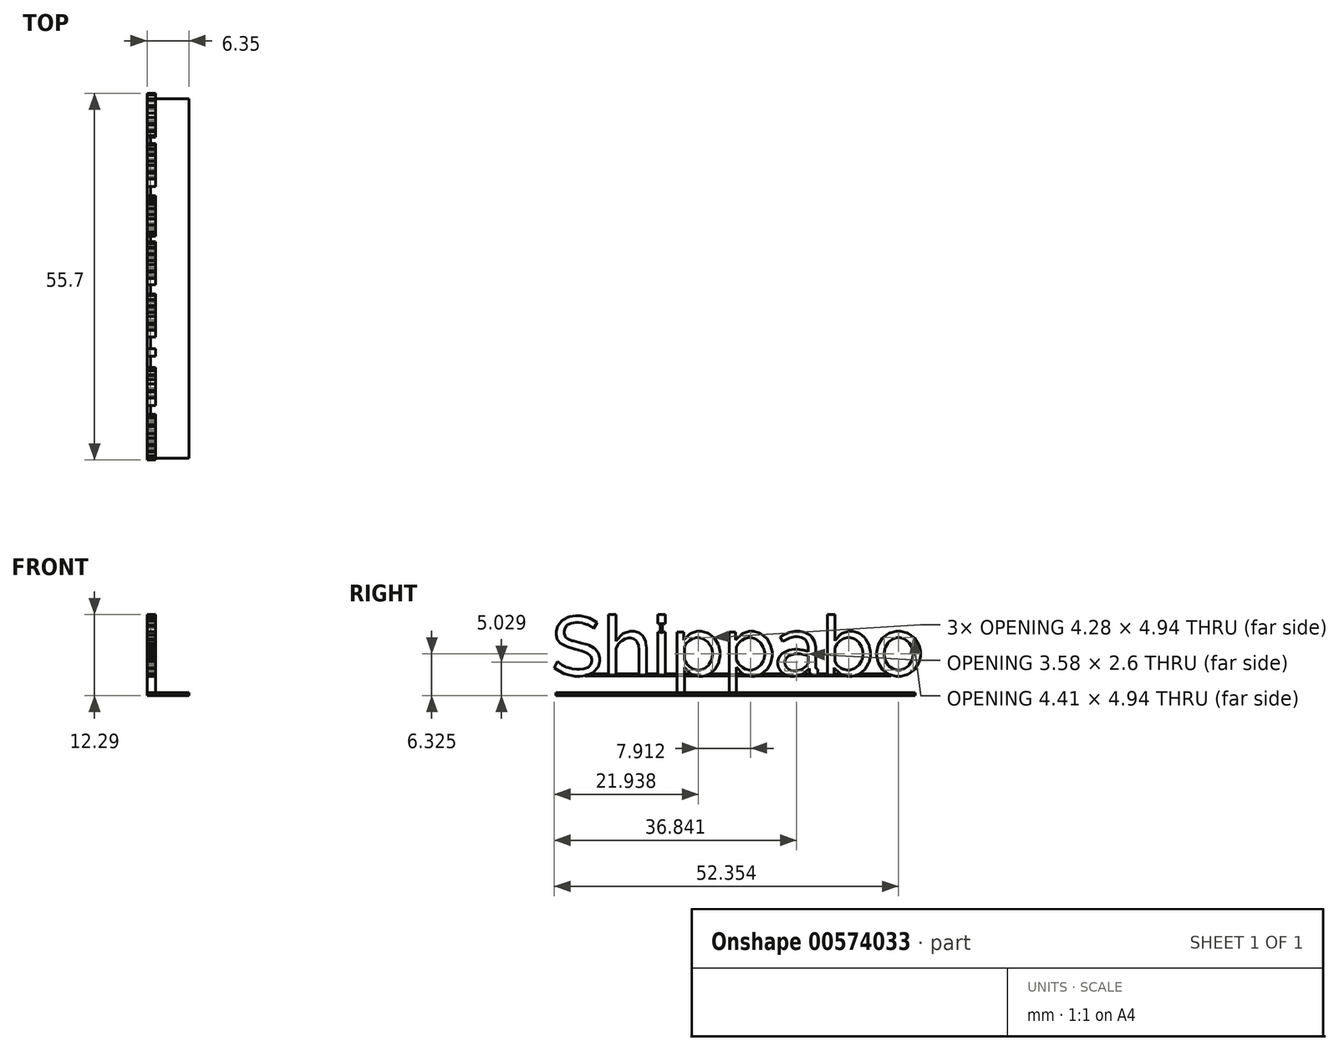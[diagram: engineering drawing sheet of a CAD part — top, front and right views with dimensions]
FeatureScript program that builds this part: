
annotation { "Feature Type Name" : "Feature", "Feature Type Description" : "" }
export const myFeature = defineFeature(function(context is Context, id is Id, definition is map)
    precondition{}
    {
        {
            var Q0;
            Q0=qCreatedBy(makeId("Right.planeOp"),FACE);
            var sketch = newSketch(context, id + "F0", { "sketchPlane" : qUnion([Q0])});
            skLineSegment(sketch, "E0", {"start": v(-21.84, 3.84) * mm, "end": v(-21.87, 3.87) * mm});
            skLineSegment(sketch, "E1", {"start": v(-21.87, 3.87) * mm, "end": v(-22.2, 4.16) * mm});
            skLineSegment(sketch, "E2", {"start": v(-22.2, 4.16) * mm, "end": v(-22.25, 4.18) * mm});
            skLineSegment(sketch, "E3", {"start": v(-22.25, 4.18) * mm, "end": v(-22.3, 4.21) * mm});
            skLineSegment(sketch, "E4", {"start": v(-22.3, 4.21) * mm, "end": v(-22.77, 4.46) * mm});
            skLineSegment(sketch, "E5", {"start": v(-22.77, 4.46) * mm, "end": v(-22.82, 4.48) * mm});
            skLineSegment(sketch, "E6", {"start": v(-22.82, 4.48) * mm, "end": v(-22.88, 4.5) * mm});
            skLineSegment(sketch, "E7", {"start": v(-22.88, 4.5) * mm, "end": v(-23.45, 4.68) * mm});
            skLineSegment(sketch, "E8", {"start": v(-23.45, 4.68) * mm, "end": v(-23.51, 4.7) * mm});
            skLineSegment(sketch, "E9", {"start": v(-23.51, 4.7) * mm, "end": v(-23.58, 4.71) * mm});
            skLineSegment(sketch, "E10", {"start": v(-23.58, 4.71) * mm, "end": v(-24.12, 4.78) * mm});
            skLineSegment(sketch, "E11", {"start": v(-24.12, 4.78) * mm, "end": v(-24.3, 4.78) * mm});
            skLineSegment(sketch, "E12", {"start": v(-24.3, 4.78) * mm, "end": v(-24.52, 4.78) * mm});
            skLineSegment(sketch, "E13", {"start": v(-24.52, 4.78) * mm, "end": v(-25.2, 4.68) * mm});
            skLineSegment(sketch, "E14", {"start": v(-25.2, 4.68) * mm, "end": v(-25.76, 4.45) * mm});
            skLineSegment(sketch, "E15", {"start": v(-25.76, 4.45) * mm, "end": v(-25.84, 4.39) * mm});
            skLineSegment(sketch, "E16", {"start": v(-25.84, 4.39) * mm, "end": v(-25.92, 4.32) * mm});
            skLineSegment(sketch, "E17", {"start": v(-25.92, 4.32) * mm, "end": v(-26.2, 3.92) * mm});
            skLineSegment(sketch, "E18", {"start": v(-26.2, 3.92) * mm, "end": v(-26.33, 3.46) * mm});
            skLineSegment(sketch, "E19", {"start": v(-26.33, 3.46) * mm, "end": v(-26.33, 3.3) * mm});
            skLineSegment(sketch, "E20", {"start": v(-26.33, 3.3) * mm, "end": v(-26.33, 3.16) * mm});
            skLineSegment(sketch, "E21", {"start": v(-26.33, 3.16) * mm, "end": v(-26.21, 2.74) * mm});
            skLineSegment(sketch, "E22", {"start": v(-26.21, 2.74) * mm, "end": v(-26.19, 2.7) * mm});
            skLineSegment(sketch, "E23", {"start": v(-26.19, 2.7) * mm, "end": v(-26.16, 2.66) * mm});
            skLineSegment(sketch, "E24", {"start": v(-26.16, 2.66) * mm, "end": v(-25.8, 2.31) * mm});
            skLineSegment(sketch, "E25", {"start": v(-25.8, 2.31) * mm, "end": v(-25.75, 2.29) * mm});
            skLineSegment(sketch, "E26", {"start": v(-25.75, 2.29) * mm, "end": v(-25.7, 2.26) * mm});
            skLineSegment(sketch, "E27", {"start": v(-25.7, 2.26) * mm, "end": v(-25.08, 2) * mm});
            skLineSegment(sketch, "E28", {"start": v(-25.08, 2) * mm, "end": v(-25, 1.99) * mm});
            skLineSegment(sketch, "E29", {"start": v(-25, 1.99) * mm, "end": v(-24.93, 1.97) * mm});
            skLineSegment(sketch, "E30", {"start": v(-24.93, 1.97) * mm, "end": v(-24.05, 1.74) * mm});
            skLineSegment(sketch, "E31", {"start": v(-24.05, 1.74) * mm, "end": v(-23.95, 1.72) * mm});
            skLineSegment(sketch, "E32", {"start": v(-23.95, 1.72) * mm, "end": v(-23.84, 1.7) * mm});
            skLineSegment(sketch, "E33", {"start": v(-23.84, 1.7) * mm, "end": v(-22.78, 1.4) * mm});
            skLineSegment(sketch, "E34", {"start": v(-22.78, 1.4) * mm, "end": v(-22.69, 1.37) * mm});
            skLineSegment(sketch, "E35", {"start": v(-22.69, 1.37) * mm, "end": v(-22.6, 1.34) * mm});
            skLineSegment(sketch, "E36", {"start": v(-22.6, 1.34) * mm, "end": v(-21.8, 0.93) * mm});
            skLineSegment(sketch, "E37", {"start": v(-21.8, 0.93) * mm, "end": v(-21.72, 0.88) * mm});
            skLineSegment(sketch, "E38", {"start": v(-21.72, 0.88) * mm, "end": v(-21.66, 0.83) * mm});
            skLineSegment(sketch, "E39", {"start": v(-21.66, 0.83) * mm, "end": v(-21.15, 0.24) * mm});
            skLineSegment(sketch, "E40", {"start": v(-21.15, 0.24) * mm, "end": v(-21.11, 0.17) * mm});
            skLineSegment(sketch, "E41", {"start": v(-21.11, 0.17) * mm, "end": v(-21.08, 0.1) * mm});
            skLineSegment(sketch, "E42", {"start": v(-21.08, 0.1) * mm, "end": v(-20.9, -0.62) * mm});
            skLineSegment(sketch, "E43", {"start": v(-20.9, -0.62) * mm, "end": v(-20.9, -0.86) * mm});
            skLineSegment(sketch, "E44", {"start": v(-20.9, -0.86) * mm, "end": v(-20.9, -1.14) * mm});
            skLineSegment(sketch, "E45", {"start": v(-20.9, -1.14) * mm, "end": v(-21.12, -1.9) * mm});
            skLineSegment(sketch, "E46", {"start": v(-21.12, -1.9) * mm, "end": v(-21.16, -1.98) * mm});
            skLineSegment(sketch, "E47", {"start": v(-21.16, -1.98) * mm, "end": v(-21.2, -2.06) * mm});
            skLineSegment(sketch, "E48", {"start": v(-21.2, -2.06) * mm, "end": v(-21.78, -2.72) * mm});
            skLineSegment(sketch, "E49", {"start": v(-21.78, -2.72) * mm, "end": v(-21.85, -2.77) * mm});
            skLineSegment(sketch, "E50", {"start": v(-21.85, -2.77) * mm, "end": v(-21.92, -2.82) * mm});
            skLineSegment(sketch, "E51", {"start": v(-21.92, -2.82) * mm, "end": v(-22.79, -3.2) * mm});
            skLineSegment(sketch, "E52", {"start": v(-22.79, -3.2) * mm, "end": v(-22.89, -3.23) * mm});
            skLineSegment(sketch, "E53", {"start": v(-22.89, -3.23) * mm, "end": v(-22.99, -3.25) * mm});
            skLineSegment(sketch, "E54", {"start": v(-22.99, -3.25) * mm, "end": v(-23.88, -3.37) * mm});
            skLineSegment(sketch, "E55", {"start": v(-23.88, -3.37) * mm, "end": v(-24.18, -3.37) * mm});
            skLineSegment(sketch, "E56", {"start": v(-24.18, -3.37) * mm, "end": v(-24.68, -3.37) * mm});
            skLineSegment(sketch, "E57", {"start": v(-24.68, -3.37) * mm, "end": v(-26, -3.1) * mm});
            skLineSegment(sketch, "E58", {"start": v(-26, -3.1) * mm, "end": v(-26.16, -3.05) * mm});
            skLineSegment(sketch, "E59", {"start": v(-26.16, -3.05) * mm, "end": v(-26.31, -3) * mm});
            skLineSegment(sketch, "E60", {"start": v(-26.31, -3) * mm, "end": v(-27.72, -2.2) * mm});
            skLineSegment(sketch, "E61", {"start": v(-27.72, -2.2) * mm, "end": v(-27.85, -2.1) * mm});
            skLineSegment(sketch, "E62", {"start": v(-27.85, -2.1) * mm, "end": v(-27.3, -1.14) * mm});
            skLineSegment(sketch, "E63", {"start": v(-27.3, -1.14) * mm, "end": v(-27.27, -1.17) * mm});
            skLineSegment(sketch, "E64", {"start": v(-27.27, -1.17) * mm, "end": v(-26.83, -1.53) * mm});
            skLineSegment(sketch, "E65", {"start": v(-26.83, -1.53) * mm, "end": v(-26.78, -1.57) * mm});
            skLineSegment(sketch, "E66", {"start": v(-26.78, -1.57) * mm, "end": v(-26.72, -1.6) * mm});
            skLineSegment(sketch, "E67", {"start": v(-26.72, -1.6) * mm, "end": v(-26.1, -1.93) * mm});
            skLineSegment(sketch, "E68", {"start": v(-26.1, -1.93) * mm, "end": v(-26.04, -1.96) * mm});
            skLineSegment(sketch, "E69", {"start": v(-26.04, -1.96) * mm, "end": v(-25.97, -1.98) * mm});
            skLineSegment(sketch, "E70", {"start": v(-25.97, -1.98) * mm, "end": v(-25.23, -2.22) * mm});
            skLineSegment(sketch, "E71", {"start": v(-25.23, -2.22) * mm, "end": v(-25.15, -2.24) * mm});
            skLineSegment(sketch, "E72", {"start": v(-25.15, -2.24) * mm, "end": v(-25.07, -2.25) * mm});
            skLineSegment(sketch, "E73", {"start": v(-25.07, -2.25) * mm, "end": v(-24.39, -2.34) * mm});
            skLineSegment(sketch, "E74", {"start": v(-24.39, -2.34) * mm, "end": v(-24.16, -2.34) * mm});
            skLineSegment(sketch, "E75", {"start": v(-24.16, -2.34) * mm, "end": v(-23.94, -2.34) * mm});
            skLineSegment(sketch, "E76", {"start": v(-23.94, -2.34) * mm, "end": v(-23.3, -2.26) * mm});
            skLineSegment(sketch, "E77", {"start": v(-23.3, -2.26) * mm, "end": v(-22.75, -2.06) * mm});
            skLineSegment(sketch, "E78", {"start": v(-22.75, -2.06) * mm, "end": v(-22.66, -2) * mm});
            skLineSegment(sketch, "E79", {"start": v(-22.66, -2) * mm, "end": v(-22.57, -1.94) * mm});
            skLineSegment(sketch, "E80", {"start": v(-22.57, -1.94) * mm, "end": v(-22.26, -1.57) * mm});
            skLineSegment(sketch, "E81", {"start": v(-22.26, -1.57) * mm, "end": v(-22.12, -1.12) * mm});
            skLineSegment(sketch, "E82", {"start": v(-22.12, -1.12) * mm, "end": v(-22.12, -0.97) * mm});
            skLineSegment(sketch, "E83", {"start": v(-22.12, -0.97) * mm, "end": v(-22.12, -0.81) * mm});
            skLineSegment(sketch, "E84", {"start": v(-22.12, -0.81) * mm, "end": v(-22.27, -0.37) * mm});
            skLineSegment(sketch, "E85", {"start": v(-22.27, -0.37) * mm, "end": v(-22.3, -0.33) * mm});
            skLineSegment(sketch, "E86", {"start": v(-22.3, -0.33) * mm, "end": v(-22.32, -0.29) * mm});
            skLineSegment(sketch, "E87", {"start": v(-22.32, -0.29) * mm, "end": v(-22.74, 0.09) * mm});
            skLineSegment(sketch, "E88", {"start": v(-22.74, 0.09) * mm, "end": v(-22.8, 0.12) * mm});
            skLineSegment(sketch, "E89", {"start": v(-22.8, 0.12) * mm, "end": v(-22.85, 0.15) * mm});
            skLineSegment(sketch, "E90", {"start": v(-22.85, 0.15) * mm, "end": v(-23.53, 0.43) * mm});
            skLineSegment(sketch, "E91", {"start": v(-23.53, 0.43) * mm, "end": v(-23.62, 0.46) * mm});
            skLineSegment(sketch, "E92", {"start": v(-23.62, 0.46) * mm, "end": v(-23.7, 0.48) * mm});
            skLineSegment(sketch, "E93", {"start": v(-23.7, 0.48) * mm, "end": v(-24.62, 0.73) * mm});
            skLineSegment(sketch, "E94", {"start": v(-24.62, 0.73) * mm, "end": v(-24.73, 0.76) * mm});
            skLineSegment(sketch, "E95", {"start": v(-24.73, 0.76) * mm, "end": v(-24.84, 0.78) * mm});
            skLineSegment(sketch, "E96", {"start": v(-24.84, 0.78) * mm, "end": v(-25.85, 1.08) * mm});
            skLineSegment(sketch, "E97", {"start": v(-25.85, 1.08) * mm, "end": v(-25.93, 1.11) * mm});
            skLineSegment(sketch, "E98", {"start": v(-25.93, 1.11) * mm, "end": v(-26.02, 1.14) * mm});
            skLineSegment(sketch, "E99", {"start": v(-26.02, 1.14) * mm, "end": v(-26.74, 1.52) * mm});
            skLineSegment(sketch, "E100", {"start": v(-26.74, 1.52) * mm, "end": v(-26.8, 1.57) * mm});
            skLineSegment(sketch, "E101", {"start": v(-26.8, 1.57) * mm, "end": v(-26.86, 1.61) * mm});
            skLineSegment(sketch, "E102", {"start": v(-26.86, 1.61) * mm, "end": v(-27.3, 2.15) * mm});
            skLineSegment(sketch, "E103", {"start": v(-27.3, 2.15) * mm, "end": v(-27.33, 2.22) * mm});
            skLineSegment(sketch, "E104", {"start": v(-27.33, 2.22) * mm, "end": v(-27.36, 2.28) * mm});
            skLineSegment(sketch, "E105", {"start": v(-27.36, 2.28) * mm, "end": v(-27.5, 2.92) * mm});
            skLineSegment(sketch, "E106", {"start": v(-27.5, 2.92) * mm, "end": v(-27.5, 3.13) * mm});
            skLineSegment(sketch, "E107", {"start": v(-27.5, 3.13) * mm, "end": v(-27.5, 3.42) * mm});
            skLineSegment(sketch, "E108", {"start": v(-27.5, 3.42) * mm, "end": v(-27.3, 4.2) * mm});
            skLineSegment(sketch, "E109", {"start": v(-27.3, 4.2) * mm, "end": v(-27.27, 4.27) * mm});
            skLineSegment(sketch, "E110", {"start": v(-27.27, 4.27) * mm, "end": v(-27.23, 4.36) * mm});
            skLineSegment(sketch, "E111", {"start": v(-27.23, 4.36) * mm, "end": v(-26.67, 5.06) * mm});
            skLineSegment(sketch, "E112", {"start": v(-26.67, 5.06) * mm, "end": v(-26.6, 5.11) * mm});
            skLineSegment(sketch, "E113", {"start": v(-26.6, 5.11) * mm, "end": v(-26.52, 5.17) * mm});
            skLineSegment(sketch, "E114", {"start": v(-26.52, 5.17) * mm, "end": v(-25.67, 5.6) * mm});
            skLineSegment(sketch, "E115", {"start": v(-25.67, 5.6) * mm, "end": v(-25.57, 5.63) * mm});
            skLineSegment(sketch, "E116", {"start": v(-25.57, 5.63) * mm, "end": v(-25.47, 5.65) * mm});
            skLineSegment(sketch, "E117", {"start": v(-25.47, 5.65) * mm, "end": v(-24.57, 5.8) * mm});
            skLineSegment(sketch, "E118", {"start": v(-24.57, 5.8) * mm, "end": v(-24.27, 5.8) * mm});
            skLineSegment(sketch, "E119", {"start": v(-24.27, 5.8) * mm, "end": v(-23.86, 5.8) * mm});
            skLineSegment(sketch, "E120", {"start": v(-23.86, 5.8) * mm, "end": v(-22.74, 5.57) * mm});
            skLineSegment(sketch, "E121", {"start": v(-22.74, 5.57) * mm, "end": v(-22.62, 5.52) * mm});
            skLineSegment(sketch, "E122", {"start": v(-22.62, 5.52) * mm, "end": v(-22.5, 5.47) * mm});
            skLineSegment(sketch, "E123", {"start": v(-22.5, 5.47) * mm, "end": v(-21.4, 4.85) * mm});
            skLineSegment(sketch, "E124", {"start": v(-21.4, 4.85) * mm, "end": v(-21.3, 4.77) * mm});
            skLineSegment(sketch, "E125", {"start": v(-21.3, 4.77) * mm, "end": v(-21.84, 3.84) * mm});
            skLineSegment(sketch, "E126", {"start": v(-13.83, -3.28) * mm, "end": v(-14.95, -3.28) * mm});
            skLineSegment(sketch, "E127", {"start": v(-14.95, -3.28) * mm, "end": v(-14.95, 0.43) * mm});
            skLineSegment(sketch, "E128", {"start": v(-14.95, 0.43) * mm, "end": v(-14.95, 0.65) * mm});
            skLineSegment(sketch, "E129", {"start": v(-14.95, 0.65) * mm, "end": v(-15.04, 1.32) * mm});
            skLineSegment(sketch, "E130", {"start": v(-15.04, 1.32) * mm, "end": v(-15.24, 1.87) * mm});
            skLineSegment(sketch, "E131", {"start": v(-15.24, 1.87) * mm, "end": v(-15.3, 1.96) * mm});
            skLineSegment(sketch, "E132", {"start": v(-15.3, 1.96) * mm, "end": v(-15.36, 2.04) * mm});
            skLineSegment(sketch, "E133", {"start": v(-15.36, 2.04) * mm, "end": v(-15.74, 2.33) * mm});
            skLineSegment(sketch, "E134", {"start": v(-15.74, 2.33) * mm, "end": v(-16.2, 2.46) * mm});
            skLineSegment(sketch, "E135", {"start": v(-16.2, 2.46) * mm, "end": v(-16.34, 2.46) * mm});
            skLineSegment(sketch, "E136", {"start": v(-16.34, 2.46) * mm, "end": v(-16.51, 2.46) * mm});
            skLineSegment(sketch, "E137", {"start": v(-16.51, 2.46) * mm, "end": v(-16.95, 2.35) * mm});
            skLineSegment(sketch, "E138", {"start": v(-16.95, 2.35) * mm, "end": v(-17, 2.32) * mm});
            skLineSegment(sketch, "E139", {"start": v(-17, 2.32) * mm, "end": v(-17.06, 2.3) * mm});
            skLineSegment(sketch, "E140", {"start": v(-17.06, 2.3) * mm, "end": v(-17.57, 2) * mm});
            skLineSegment(sketch, "E141", {"start": v(-17.57, 2) * mm, "end": v(-17.62, 1.96) * mm});
            skLineSegment(sketch, "E142", {"start": v(-17.62, 1.96) * mm, "end": v(-17.67, 1.92) * mm});
            skLineSegment(sketch, "E143", {"start": v(-17.67, 1.92) * mm, "end": v(-18.1, 1.47) * mm});
            skLineSegment(sketch, "E144", {"start": v(-18.1, 1.47) * mm, "end": v(-18.13, 1.42) * mm});
            skLineSegment(sketch, "E145", {"start": v(-18.13, 1.42) * mm, "end": v(-18.17, 1.36) * mm});
            skLineSegment(sketch, "E146", {"start": v(-18.17, 1.36) * mm, "end": v(-18.45, 0.78) * mm});
            skLineSegment(sketch, "E147", {"start": v(-18.45, 0.78) * mm, "end": v(-18.47, 0.72) * mm});
            skLineSegment(sketch, "E148", {"start": v(-18.47, 0.72) * mm, "end": v(-18.47, -3.28) * mm});
            skLineSegment(sketch, "E149", {"start": v(-18.47, -3.28) * mm, "end": v(-19.58, -3.28) * mm});
            skLineSegment(sketch, "E150", {"start": v(-19.58, -3.28) * mm, "end": v(-19.58, 5.99) * mm});
            skLineSegment(sketch, "E151", {"start": v(-19.58, 5.99) * mm, "end": v(-18.47, 5.99) * mm});
            skLineSegment(sketch, "E152", {"start": v(-18.47, 5.99) * mm, "end": v(-18.47, 1.92) * mm});
            skLineSegment(sketch, "E153", {"start": v(-18.47, 1.92) * mm, "end": v(-18.4, 2.05) * mm});
            skLineSegment(sketch, "E154", {"start": v(-18.4, 2.05) * mm, "end": v(-17.51, 2.99) * mm});
            skLineSegment(sketch, "E155", {"start": v(-17.51, 2.99) * mm, "end": v(-17.4, 3.05) * mm});
            skLineSegment(sketch, "E156", {"start": v(-17.4, 3.05) * mm, "end": v(-17.29, 3.12) * mm});
            skLineSegment(sketch, "E157", {"start": v(-17.29, 3.12) * mm, "end": v(-16.27, 3.46) * mm});
            skLineSegment(sketch, "E158", {"start": v(-16.27, 3.46) * mm, "end": v(-15.93, 3.46) * mm});
            skLineSegment(sketch, "E159", {"start": v(-15.93, 3.46) * mm, "end": v(-15.68, 3.46) * mm});
            skLineSegment(sketch, "E160", {"start": v(-15.68, 3.46) * mm, "end": v(-15, 3.28) * mm});
            skLineSegment(sketch, "E161", {"start": v(-15, 3.28) * mm, "end": v(-14.94, 3.24) * mm});
            skLineSegment(sketch, "E162", {"start": v(-14.94, 3.24) * mm, "end": v(-14.87, 3.2) * mm});
            skLineSegment(sketch, "E163", {"start": v(-14.87, 3.2) * mm, "end": v(-14.33, 2.72) * mm});
            skLineSegment(sketch, "E164", {"start": v(-14.33, 2.72) * mm, "end": v(-14.29, 2.66) * mm});
            skLineSegment(sketch, "E165", {"start": v(-14.29, 2.66) * mm, "end": v(-14.25, 2.6) * mm});
            skLineSegment(sketch, "E166", {"start": v(-14.25, 2.6) * mm, "end": v(-13.96, 1.86) * mm});
            skLineSegment(sketch, "E167", {"start": v(-13.96, 1.86) * mm, "end": v(-13.94, 1.78) * mm});
            skLineSegment(sketch, "E168", {"start": v(-13.94, 1.78) * mm, "end": v(-13.92, 1.7) * mm});
            skLineSegment(sketch, "E169", {"start": v(-13.92, 1.7) * mm, "end": v(-13.83, 0.93) * mm});
            skLineSegment(sketch, "E170", {"start": v(-13.83, 0.93) * mm, "end": v(-13.83, 0.68) * mm});
            skLineSegment(sketch, "E171", {"start": v(-13.83, 0.68) * mm, "end": v(-13.83, -3.28) * mm});
            skLineSegment(sketch, "E172", {"start": v(-12.1, -3.28) * mm, "end": v(-12.1, 3.35) * mm});
            skLineSegment(sketch, "E173", {"start": v(-12.1, 3.35) * mm, "end": v(-10.97, 3.35) * mm});
            skLineSegment(sketch, "E174", {"start": v(-10.97, 3.35) * mm, "end": v(-10.97, -3.28) * mm});
            skLineSegment(sketch, "E175", {"start": v(-10.97, -3.28) * mm, "end": v(-12.1, -3.28) * mm});
            skLineSegment(sketch, "E176", {"start": v(-12.1, 4.6) * mm, "end": v(-12.1, 5.99) * mm});
            skLineSegment(sketch, "E177", {"start": v(-12.1, 5.99) * mm, "end": v(-10.97, 5.99) * mm});
            skLineSegment(sketch, "E178", {"start": v(-10.97, 5.99) * mm, "end": v(-10.97, 4.6) * mm});
            skLineSegment(sketch, "E179", {"start": v(-10.97, 4.6) * mm, "end": v(-12.1, 4.6) * mm});
            skLineSegment(sketch, "E180", {"start": v(-5.6, -3.4) * mm, "end": v(-5.96, -3.4) * mm});
            skLineSegment(sketch, "E181", {"start": v(-5.96, -3.4) * mm, "end": v(-6.95, -3.07) * mm});
            skLineSegment(sketch, "E182", {"start": v(-6.95, -3.07) * mm, "end": v(-7.06, -3) * mm});
            skLineSegment(sketch, "E183", {"start": v(-7.06, -3) * mm, "end": v(-7.16, -2.94) * mm});
            skLineSegment(sketch, "E184", {"start": v(-7.16, -2.94) * mm, "end": v(-8, -2.08) * mm});
            skLineSegment(sketch, "E185", {"start": v(-8, -2.08) * mm, "end": v(-8.05, -1.98) * mm});
            skLineSegment(sketch, "E186", {"start": v(-8.05, -1.98) * mm, "end": v(-8.05, -5.99) * mm});
            skLineSegment(sketch, "E187", {"start": v(-8.05, -5.99) * mm, "end": v(-9.17, -5.99) * mm});
            skLineSegment(sketch, "E188", {"start": v(-9.17, -5.99) * mm, "end": v(-9.17, 3.35) * mm});
            skLineSegment(sketch, "E189", {"start": v(-9.17, 3.35) * mm, "end": v(-8.18, 3.35) * mm});
            skLineSegment(sketch, "E190", {"start": v(-8.18, 3.35) * mm, "end": v(-8.18, 2.1) * mm});
            skLineSegment(sketch, "E191", {"start": v(-8.18, 2.1) * mm, "end": v(-8.11, 2.2) * mm});
            skLineSegment(sketch, "E192", {"start": v(-8.11, 2.2) * mm, "end": v(-7.26, 3.02) * mm});
            skLineSegment(sketch, "E193", {"start": v(-7.26, 3.02) * mm, "end": v(-7.16, 3.09) * mm});
            skLineSegment(sketch, "E194", {"start": v(-7.16, 3.09) * mm, "end": v(-7.05, 3.15) * mm});
            skLineSegment(sketch, "E195", {"start": v(-7.05, 3.15) * mm, "end": v(-6.09, 3.46) * mm});
            skLineSegment(sketch, "E196", {"start": v(-6.09, 3.46) * mm, "end": v(-5.77, 3.46) * mm});
            skLineSegment(sketch, "E197", {"start": v(-5.77, 3.46) * mm, "end": v(-5.45, 3.46) * mm});
            skLineSegment(sketch, "E198", {"start": v(-5.45, 3.46) * mm, "end": v(-4.6, 3.23) * mm});
            skLineSegment(sketch, "E199", {"start": v(-4.6, 3.23) * mm, "end": v(-4.5, 3.18) * mm});
            skLineSegment(sketch, "E200", {"start": v(-4.5, 3.18) * mm, "end": v(-4.41, 3.14) * mm});
            skLineSegment(sketch, "E201", {"start": v(-4.41, 3.14) * mm, "end": v(-3.59, 2.5) * mm});
            skLineSegment(sketch, "E202", {"start": v(-3.59, 2.5) * mm, "end": v(-3.52, 2.43) * mm});
            skLineSegment(sketch, "E203", {"start": v(-3.52, 2.43) * mm, "end": v(-3.45, 2.35) * mm});
            skLineSegment(sketch, "E204", {"start": v(-3.45, 2.35) * mm, "end": v(-2.9, 1.43) * mm});
            skLineSegment(sketch, "E205", {"start": v(-2.9, 1.43) * mm, "end": v(-2.86, 1.33) * mm});
            skLineSegment(sketch, "E206", {"start": v(-2.86, 1.33) * mm, "end": v(-2.82, 1.22) * mm});
            skLineSegment(sketch, "E207", {"start": v(-2.82, 1.22) * mm, "end": v(-2.63, 0.33) * mm});
            skLineSegment(sketch, "E208", {"start": v(-2.63, 0.33) * mm, "end": v(-2.63, 0.03) * mm});
            skLineSegment(sketch, "E209", {"start": v(-2.63, 0.03) * mm, "end": v(-2.63, -0.3) * mm});
            skLineSegment(sketch, "E210", {"start": v(-2.63, -0.3) * mm, "end": v(-2.8, -1.2) * mm});
            skLineSegment(sketch, "E211", {"start": v(-2.8, -1.2) * mm, "end": v(-2.84, -1.3) * mm});
            skLineSegment(sketch, "E212", {"start": v(-2.84, -1.3) * mm, "end": v(-2.88, -1.41) * mm});
            skLineSegment(sketch, "E213", {"start": v(-2.88, -1.41) * mm, "end": v(-3.39, -2.32) * mm});
            skLineSegment(sketch, "E214", {"start": v(-3.39, -2.32) * mm, "end": v(-3.45, -2.4) * mm});
            skLineSegment(sketch, "E215", {"start": v(-3.45, -2.4) * mm, "end": v(-3.52, -2.48) * mm});
            skLineSegment(sketch, "E216", {"start": v(-3.52, -2.48) * mm, "end": v(-4.3, -3.1) * mm});
            skLineSegment(sketch, "E217", {"start": v(-4.3, -3.1) * mm, "end": v(-4.4, -3.14) * mm});
            skLineSegment(sketch, "E218", {"start": v(-4.4, -3.14) * mm, "end": v(-4.49, -3.18) * mm});
            skLineSegment(sketch, "E219", {"start": v(-4.49, -3.18) * mm, "end": v(-5.32, -3.4) * mm});
            skLineSegment(sketch, "E220", {"start": v(-5.32, -3.4) * mm, "end": v(-5.6, -3.4) * mm});
            skLineSegment(sketch, "E221", {"start": v(-5.94, -2.45) * mm, "end": v(-5.72, -2.45) * mm});
            skLineSegment(sketch, "E222", {"start": v(-5.72, -2.45) * mm, "end": v(-5.12, -2.27) * mm});
            skLineSegment(sketch, "E223", {"start": v(-5.12, -2.27) * mm, "end": v(-5.05, -2.24) * mm});
            skLineSegment(sketch, "E224", {"start": v(-5.05, -2.24) * mm, "end": v(-4.98, -2.2) * mm});
            skLineSegment(sketch, "E225", {"start": v(-4.98, -2.2) * mm, "end": v(-4.41, -1.73) * mm});
            skLineSegment(sketch, "E226", {"start": v(-4.41, -1.73) * mm, "end": v(-4.36, -1.68) * mm});
            skLineSegment(sketch, "E227", {"start": v(-4.36, -1.68) * mm, "end": v(-4.32, -1.62) * mm});
            skLineSegment(sketch, "E228", {"start": v(-4.32, -1.62) * mm, "end": v(-3.95, -0.96) * mm});
            skLineSegment(sketch, "E229", {"start": v(-3.95, -0.96) * mm, "end": v(-3.92, -0.88) * mm});
            skLineSegment(sketch, "E230", {"start": v(-3.92, -0.88) * mm, "end": v(-3.9, -0.8) * mm});
            skLineSegment(sketch, "E231", {"start": v(-3.9, -0.8) * mm, "end": v(-3.77, -0.18) * mm});
            skLineSegment(sketch, "E232", {"start": v(-3.77, -0.18) * mm, "end": v(-3.77, 0.03) * mm});
            skLineSegment(sketch, "E233", {"start": v(-3.77, 0.03) * mm, "end": v(-3.77, 0.27) * mm});
            skLineSegment(sketch, "E234", {"start": v(-3.77, 0.27) * mm, "end": v(-3.92, 0.9) * mm});
            skLineSegment(sketch, "E235", {"start": v(-3.92, 0.9) * mm, "end": v(-3.95, 0.98) * mm});
            skLineSegment(sketch, "E236", {"start": v(-3.95, 0.98) * mm, "end": v(-3.98, 1.05) * mm});
            skLineSegment(sketch, "E237", {"start": v(-3.98, 1.05) * mm, "end": v(-4.38, 1.7) * mm});
            skLineSegment(sketch, "E238", {"start": v(-4.38, 1.7) * mm, "end": v(-4.43, 1.76) * mm});
            skLineSegment(sketch, "E239", {"start": v(-4.43, 1.76) * mm, "end": v(-4.48, 1.82) * mm});
            skLineSegment(sketch, "E240", {"start": v(-4.48, 1.82) * mm, "end": v(-5.08, 2.27) * mm});
            skLineSegment(sketch, "E241", {"start": v(-5.08, 2.27) * mm, "end": v(-5.15, 2.3) * mm});
            skLineSegment(sketch, "E242", {"start": v(-5.15, 2.3) * mm, "end": v(-5.22, 2.33) * mm});
            skLineSegment(sketch, "E243", {"start": v(-5.22, 2.33) * mm, "end": v(-5.84, 2.5) * mm});
            skLineSegment(sketch, "E244", {"start": v(-5.84, 2.5) * mm, "end": v(-6.05, 2.5) * mm});
            skLineSegment(sketch, "E245", {"start": v(-6.05, 2.5) * mm, "end": v(-6.2, 2.5) * mm});
            skLineSegment(sketch, "E246", {"start": v(-6.2, 2.5) * mm, "end": v(-6.62, 2.4) * mm});
            skLineSegment(sketch, "E247", {"start": v(-6.62, 2.4) * mm, "end": v(-6.67, 2.38) * mm});
            skLineSegment(sketch, "E248", {"start": v(-6.67, 2.38) * mm, "end": v(-6.73, 2.36) * mm});
            skLineSegment(sketch, "E249", {"start": v(-6.73, 2.36) * mm, "end": v(-7.24, 2.09) * mm});
            skLineSegment(sketch, "E250", {"start": v(-7.24, 2.09) * mm, "end": v(-7.28, 2.06) * mm});
            skLineSegment(sketch, "E251", {"start": v(-7.28, 2.06) * mm, "end": v(-7.33, 2.03) * mm});
            skLineSegment(sketch, "E252", {"start": v(-7.33, 2.03) * mm, "end": v(-7.74, 1.63) * mm});
            skLineSegment(sketch, "E253", {"start": v(-7.74, 1.63) * mm, "end": v(-7.78, 1.59) * mm});
            skLineSegment(sketch, "E254", {"start": v(-7.78, 1.59) * mm, "end": v(-7.81, 1.54) * mm});
            skLineSegment(sketch, "E255", {"start": v(-7.81, 1.54) * mm, "end": v(-8.04, 1.06) * mm});
            skLineSegment(sketch, "E256", {"start": v(-8.04, 1.06) * mm, "end": v(-8.05, 1) * mm});
            skLineSegment(sketch, "E257", {"start": v(-8.05, 1) * mm, "end": v(-8.05, -0.88) * mm});
            skLineSegment(sketch, "E258", {"start": v(-8.05, -0.88) * mm, "end": v(-8.03, -0.94) * mm});
            skLineSegment(sketch, "E259", {"start": v(-8.03, -0.94) * mm, "end": v(-7.73, -1.45) * mm});
            skLineSegment(sketch, "E260", {"start": v(-7.73, -1.45) * mm, "end": v(-7.7, -1.5) * mm});
            skLineSegment(sketch, "E261", {"start": v(-7.7, -1.5) * mm, "end": v(-7.66, -1.55) * mm});
            skLineSegment(sketch, "E262", {"start": v(-7.66, -1.55) * mm, "end": v(-7.25, -1.96) * mm});
            skLineSegment(sketch, "E263", {"start": v(-7.25, -1.96) * mm, "end": v(-7.2, -2) * mm});
            skLineSegment(sketch, "E264", {"start": v(-7.2, -2) * mm, "end": v(-7.15, -2.03) * mm});
            skLineSegment(sketch, "E265", {"start": v(-7.15, -2.03) * mm, "end": v(-6.66, -2.3) * mm});
            skLineSegment(sketch, "E266", {"start": v(-6.66, -2.3) * mm, "end": v(-6.6, -2.32) * mm});
            skLineSegment(sketch, "E267", {"start": v(-6.6, -2.32) * mm, "end": v(-6.55, -2.34) * mm});
            skLineSegment(sketch, "E268", {"start": v(-6.55, -2.34) * mm, "end": v(-6.1, -2.45) * mm});
            skLineSegment(sketch, "E269", {"start": v(-6.1, -2.45) * mm, "end": v(-5.94, -2.45) * mm});
            skLineSegment(sketch, "E270", {"start": v(2.31, -3.4) * mm, "end": v(1.95, -3.4) * mm});
            skLineSegment(sketch, "E271", {"start": v(1.95, -3.4) * mm, "end": v(0.96, -3.07) * mm});
            skLineSegment(sketch, "E272", {"start": v(0.96, -3.07) * mm, "end": v(0.86, -3) * mm});
            skLineSegment(sketch, "E273", {"start": v(0.86, -3) * mm, "end": v(0.75, -2.94) * mm});
            skLineSegment(sketch, "E274", {"start": v(0.75, -2.94) * mm, "end": v(-0.08, -2.08) * mm});
            skLineSegment(sketch, "E275", {"start": v(-0.08, -2.08) * mm, "end": v(-0.14, -1.98) * mm});
            skLineSegment(sketch, "E276", {"start": v(-0.14, -1.98) * mm, "end": v(-0.14, -5.99) * mm});
            skLineSegment(sketch, "E277", {"start": v(-0.14, -5.99) * mm, "end": v(-1.26, -5.99) * mm});
            skLineSegment(sketch, "E278", {"start": v(-1.26, -5.99) * mm, "end": v(-1.26, 3.35) * mm});
            skLineSegment(sketch, "E279", {"start": v(-1.26, 3.35) * mm, "end": v(-0.27, 3.35) * mm});
            skLineSegment(sketch, "E280", {"start": v(-0.27, 3.35) * mm, "end": v(-0.27, 2.1) * mm});
            skLineSegment(sketch, "E281", {"start": v(-0.27, 2.1) * mm, "end": v(-0.2, 2.2) * mm});
            skLineSegment(sketch, "E282", {"start": v(-0.2, 2.2) * mm, "end": v(0.65, 3.02) * mm});
            skLineSegment(sketch, "E283", {"start": v(0.65, 3.02) * mm, "end": v(0.76, 3.09) * mm});
            skLineSegment(sketch, "E284", {"start": v(0.76, 3.09) * mm, "end": v(0.86, 3.15) * mm});
            skLineSegment(sketch, "E285", {"start": v(0.86, 3.15) * mm, "end": v(1.82, 3.46) * mm});
            skLineSegment(sketch, "E286", {"start": v(1.82, 3.46) * mm, "end": v(2.15, 3.46) * mm});
            skLineSegment(sketch, "E287", {"start": v(2.15, 3.46) * mm, "end": v(2.46, 3.46) * mm});
            skLineSegment(sketch, "E288", {"start": v(2.46, 3.46) * mm, "end": v(3.3, 3.23) * mm});
            skLineSegment(sketch, "E289", {"start": v(3.3, 3.23) * mm, "end": v(3.4, 3.18) * mm});
            skLineSegment(sketch, "E290", {"start": v(3.4, 3.18) * mm, "end": v(3.5, 3.14) * mm});
            skLineSegment(sketch, "E291", {"start": v(3.5, 3.14) * mm, "end": v(4.32, 2.5) * mm});
            skLineSegment(sketch, "E292", {"start": v(4.32, 2.5) * mm, "end": v(4.4, 2.43) * mm});
            skLineSegment(sketch, "E293", {"start": v(4.4, 2.43) * mm, "end": v(4.46, 2.35) * mm});
            skLineSegment(sketch, "E294", {"start": v(4.46, 2.35) * mm, "end": v(5, 1.43) * mm});
            skLineSegment(sketch, "E295", {"start": v(5, 1.43) * mm, "end": v(5.05, 1.33) * mm});
            skLineSegment(sketch, "E296", {"start": v(5.05, 1.33) * mm, "end": v(5.09, 1.22) * mm});
            skLineSegment(sketch, "E297", {"start": v(5.09, 1.22) * mm, "end": v(5.28, 0.33) * mm});
            skLineSegment(sketch, "E298", {"start": v(5.28, 0.33) * mm, "end": v(5.28, 0.03) * mm});
            skLineSegment(sketch, "E299", {"start": v(5.28, 0.03) * mm, "end": v(5.28, -0.3) * mm});
            skLineSegment(sketch, "E300", {"start": v(5.28, -0.3) * mm, "end": v(5.1, -1.2) * mm});
            skLineSegment(sketch, "E301", {"start": v(5.1, -1.2) * mm, "end": v(5.07, -1.3) * mm});
            skLineSegment(sketch, "E302", {"start": v(5.07, -1.3) * mm, "end": v(5.03, -1.41) * mm});
            skLineSegment(sketch, "E303", {"start": v(5.03, -1.41) * mm, "end": v(4.52, -2.32) * mm});
            skLineSegment(sketch, "E304", {"start": v(4.52, -2.32) * mm, "end": v(4.46, -2.4) * mm});
            skLineSegment(sketch, "E305", {"start": v(4.46, -2.4) * mm, "end": v(4.4, -2.48) * mm});
            skLineSegment(sketch, "E306", {"start": v(4.4, -2.48) * mm, "end": v(3.6, -3.1) * mm});
            skLineSegment(sketch, "E307", {"start": v(3.6, -3.1) * mm, "end": v(3.52, -3.14) * mm});
            skLineSegment(sketch, "E308", {"start": v(3.52, -3.14) * mm, "end": v(3.43, -3.18) * mm});
            skLineSegment(sketch, "E309", {"start": v(3.43, -3.18) * mm, "end": v(2.59, -3.4) * mm});
            skLineSegment(sketch, "E310", {"start": v(2.59, -3.4) * mm, "end": v(2.31, -3.4) * mm});
            skLineSegment(sketch, "E311", {"start": v(1.97, -2.45) * mm, "end": v(2.2, -2.45) * mm});
            skLineSegment(sketch, "E312", {"start": v(2.2, -2.45) * mm, "end": v(2.8, -2.27) * mm});
            skLineSegment(sketch, "E313", {"start": v(2.8, -2.27) * mm, "end": v(2.86, -2.24) * mm});
            skLineSegment(sketch, "E314", {"start": v(2.86, -2.24) * mm, "end": v(2.93, -2.2) * mm});
            skLineSegment(sketch, "E315", {"start": v(2.93, -2.2) * mm, "end": v(3.5, -1.73) * mm});
            skLineSegment(sketch, "E316", {"start": v(3.5, -1.73) * mm, "end": v(3.55, -1.68) * mm});
            skLineSegment(sketch, "E317", {"start": v(3.55, -1.68) * mm, "end": v(3.6, -1.62) * mm});
            skLineSegment(sketch, "E318", {"start": v(3.6, -1.62) * mm, "end": v(3.96, -0.96) * mm});
            skLineSegment(sketch, "E319", {"start": v(3.96, -0.96) * mm, "end": v(3.99, -0.88) * mm});
            skLineSegment(sketch, "E320", {"start": v(3.99, -0.88) * mm, "end": v(4.01, -0.8) * mm});
            skLineSegment(sketch, "E321", {"start": v(4.01, -0.8) * mm, "end": v(4.14, -0.18) * mm});
            skLineSegment(sketch, "E322", {"start": v(4.14, -0.18) * mm, "end": v(4.14, 0.03) * mm});
            skLineSegment(sketch, "E323", {"start": v(4.14, 0.03) * mm, "end": v(4.14, 0.27) * mm});
            skLineSegment(sketch, "E324", {"start": v(4.14, 0.27) * mm, "end": v(4, 0.9) * mm});
            skLineSegment(sketch, "E325", {"start": v(4, 0.9) * mm, "end": v(3.96, 0.98) * mm});
            skLineSegment(sketch, "E326", {"start": v(3.96, 0.98) * mm, "end": v(3.93, 1.05) * mm});
            skLineSegment(sketch, "E327", {"start": v(3.93, 1.05) * mm, "end": v(3.53, 1.7) * mm});
            skLineSegment(sketch, "E328", {"start": v(3.53, 1.7) * mm, "end": v(3.48, 1.76) * mm});
            skLineSegment(sketch, "E329", {"start": v(3.48, 1.76) * mm, "end": v(3.43, 1.82) * mm});
            skLineSegment(sketch, "E330", {"start": v(3.43, 1.82) * mm, "end": v(2.83, 2.27) * mm});
            skLineSegment(sketch, "E331", {"start": v(2.83, 2.27) * mm, "end": v(2.76, 2.3) * mm});
            skLineSegment(sketch, "E332", {"start": v(2.76, 2.3) * mm, "end": v(2.7, 2.33) * mm});
            skLineSegment(sketch, "E333", {"start": v(2.7, 2.33) * mm, "end": v(2.07, 2.5) * mm});
            skLineSegment(sketch, "E334", {"start": v(2.07, 2.5) * mm, "end": v(1.87, 2.5) * mm});
            skLineSegment(sketch, "E335", {"start": v(1.87, 2.5) * mm, "end": v(1.71, 2.5) * mm});
            skLineSegment(sketch, "E336", {"start": v(1.71, 2.5) * mm, "end": v(1.3, 2.4) * mm});
            skLineSegment(sketch, "E337", {"start": v(1.3, 2.4) * mm, "end": v(1.24, 2.38) * mm});
            skLineSegment(sketch, "E338", {"start": v(1.24, 2.38) * mm, "end": v(1.18, 2.36) * mm});
            skLineSegment(sketch, "E339", {"start": v(1.18, 2.36) * mm, "end": v(0.68, 2.09) * mm});
            skLineSegment(sketch, "E340", {"start": v(0.68, 2.09) * mm, "end": v(0.63, 2.06) * mm});
            skLineSegment(sketch, "E341", {"start": v(0.63, 2.06) * mm, "end": v(0.58, 2.03) * mm});
            skLineSegment(sketch, "E342", {"start": v(0.58, 2.03) * mm, "end": v(0.17, 1.63) * mm});
            skLineSegment(sketch, "E343", {"start": v(0.17, 1.63) * mm, "end": v(0.13, 1.59) * mm});
            skLineSegment(sketch, "E344", {"start": v(0.13, 1.59) * mm, "end": v(0.1, 1.54) * mm});
            skLineSegment(sketch, "E345", {"start": v(0.1, 1.54) * mm, "end": v(-0.13, 1.06) * mm});
            skLineSegment(sketch, "E346", {"start": v(-0.13, 1.06) * mm, "end": v(-0.14, 1) * mm});
            skLineSegment(sketch, "E347", {"start": v(-0.14, 1) * mm, "end": v(-0.14, -0.88) * mm});
            skLineSegment(sketch, "E348", {"start": v(-0.14, -0.88) * mm, "end": v(-0.12, -0.94) * mm});
            skLineSegment(sketch, "E349", {"start": v(-0.12, -0.94) * mm, "end": v(0.18, -1.45) * mm});
            skLineSegment(sketch, "E350", {"start": v(0.18, -1.45) * mm, "end": v(0.22, -1.5) * mm});
            skLineSegment(sketch, "E351", {"start": v(0.22, -1.5) * mm, "end": v(0.25, -1.55) * mm});
            skLineSegment(sketch, "E352", {"start": v(0.25, -1.55) * mm, "end": v(0.66, -1.96) * mm});
            skLineSegment(sketch, "E353", {"start": v(0.66, -1.96) * mm, "end": v(0.71, -2) * mm});
            skLineSegment(sketch, "E354", {"start": v(0.71, -2) * mm, "end": v(0.76, -2.03) * mm});
            skLineSegment(sketch, "E355", {"start": v(0.76, -2.03) * mm, "end": v(1.25, -2.3) * mm});
            skLineSegment(sketch, "E356", {"start": v(1.25, -2.3) * mm, "end": v(1.3, -2.32) * mm});
            skLineSegment(sketch, "E357", {"start": v(1.3, -2.32) * mm, "end": v(1.36, -2.34) * mm});
            skLineSegment(sketch, "E358", {"start": v(1.36, -2.34) * mm, "end": v(1.81, -2.45) * mm});
            skLineSegment(sketch, "E359", {"start": v(1.81, -2.45) * mm, "end": v(1.97, -2.45) * mm});
            skLineSegment(sketch, "E360", {"start": v(8.36, -3.4) * mm, "end": v(8.14, -3.4) * mm});
            skLineSegment(sketch, "E361", {"start": v(8.14, -3.4) * mm, "end": v(7.55, -3.28) * mm});
            skLineSegment(sketch, "E362", {"start": v(7.55, -3.28) * mm, "end": v(7.48, -3.25) * mm});
            skLineSegment(sketch, "E363", {"start": v(7.48, -3.25) * mm, "end": v(7.41, -3.22) * mm});
            skLineSegment(sketch, "E364", {"start": v(7.41, -3.22) * mm, "end": v(6.83, -2.86) * mm});
            skLineSegment(sketch, "E365", {"start": v(6.83, -2.86) * mm, "end": v(6.78, -2.81) * mm});
            skLineSegment(sketch, "E366", {"start": v(6.78, -2.81) * mm, "end": v(6.72, -2.77) * mm});
            skLineSegment(sketch, "E367", {"start": v(6.72, -2.77) * mm, "end": v(6.33, -2.22) * mm});
            skLineSegment(sketch, "E368", {"start": v(6.33, -2.22) * mm, "end": v(6.3, -2.16) * mm});
            skLineSegment(sketch, "E369", {"start": v(6.3, -2.16) * mm, "end": v(6.28, -2.1) * mm});
            skLineSegment(sketch, "E370", {"start": v(6.28, -2.1) * mm, "end": v(6.13, -1.53) * mm});
            skLineSegment(sketch, "E371", {"start": v(6.13, -1.53) * mm, "end": v(6.13, -1.34) * mm});
            skLineSegment(sketch, "E372", {"start": v(6.13, -1.34) * mm, "end": v(6.13, -1.13) * mm});
            skLineSegment(sketch, "E373", {"start": v(6.13, -1.13) * mm, "end": v(6.3, -0.57) * mm});
            skLineSegment(sketch, "E374", {"start": v(6.3, -0.57) * mm, "end": v(6.34, -0.5) * mm});
            skLineSegment(sketch, "E375", {"start": v(6.34, -0.5) * mm, "end": v(6.37, -0.44) * mm});
            skLineSegment(sketch, "E376", {"start": v(6.37, -0.44) * mm, "end": v(6.85, 0.09) * mm});
            skLineSegment(sketch, "E377", {"start": v(6.85, 0.09) * mm, "end": v(6.92, 0.13) * mm});
            skLineSegment(sketch, "E378", {"start": v(6.92, 0.13) * mm, "end": v(6.98, 0.18) * mm});
            skLineSegment(sketch, "E379", {"start": v(6.98, 0.18) * mm, "end": v(7.72, 0.53) * mm});
            skLineSegment(sketch, "E380", {"start": v(7.72, 0.53) * mm, "end": v(7.8, 0.55) * mm});
            skLineSegment(sketch, "E381", {"start": v(7.8, 0.55) * mm, "end": v(7.89, 0.58) * mm});
            skLineSegment(sketch, "E382", {"start": v(7.89, 0.58) * mm, "end": v(8.67, 0.7) * mm});
            skLineSegment(sketch, "E383", {"start": v(8.67, 0.7) * mm, "end": v(8.93, 0.7) * mm});
            skLineSegment(sketch, "E384", {"start": v(8.93, 0.7) * mm, "end": v(9.17, 0.7) * mm});
            skLineSegment(sketch, "E385", {"start": v(9.17, 0.7) * mm, "end": v(9.82, 0.63) * mm});
            skLineSegment(sketch, "E386", {"start": v(9.82, 0.63) * mm, "end": v(9.9, 0.62) * mm});
            skLineSegment(sketch, "E387", {"start": v(9.9, 0.62) * mm, "end": v(9.99, 0.6) * mm});
            skLineSegment(sketch, "E388", {"start": v(9.99, 0.6) * mm, "end": v(10.72, 0.4) * mm});
            skLineSegment(sketch, "E389", {"start": v(10.72, 0.4) * mm, "end": v(10.78, 0.37) * mm});
            skLineSegment(sketch, "E390", {"start": v(10.78, 0.37) * mm, "end": v(10.78, 0.9) * mm});
            skLineSegment(sketch, "E391", {"start": v(10.78, 0.9) * mm, "end": v(10.78, 1.09) * mm});
            skLineSegment(sketch, "E392", {"start": v(10.78, 1.09) * mm, "end": v(10.67, 1.63) * mm});
            skLineSegment(sketch, "E393", {"start": v(10.67, 1.63) * mm, "end": v(10.4, 2.1) * mm});
            skLineSegment(sketch, "E394", {"start": v(10.4, 2.1) * mm, "end": v(10.33, 2.18) * mm});
            skLineSegment(sketch, "E395", {"start": v(10.33, 2.18) * mm, "end": v(10.25, 2.26) * mm});
            skLineSegment(sketch, "E396", {"start": v(10.25, 2.26) * mm, "end": v(9.77, 2.53) * mm});
            skLineSegment(sketch, "E397", {"start": v(9.77, 2.53) * mm, "end": v(9.21, 2.65) * mm});
            skLineSegment(sketch, "E398", {"start": v(9.21, 2.65) * mm, "end": v(9.03, 2.65) * mm});
            skLineSegment(sketch, "E399", {"start": v(9.03, 2.65) * mm, "end": v(8.77, 2.65) * mm});
            skLineSegment(sketch, "E400", {"start": v(8.77, 2.65) * mm, "end": v(8, 2.45) * mm});
            skLineSegment(sketch, "E401", {"start": v(8, 2.45) * mm, "end": v(7.1, 2) * mm});
            skLineSegment(sketch, "E402", {"start": v(7.1, 2) * mm, "end": v(6.92, 1.87) * mm});
            skLineSegment(sketch, "E403", {"start": v(6.92, 1.87) * mm, "end": v(6.55, 2.6) * mm});
            skLineSegment(sketch, "E404", {"start": v(6.55, 2.6) * mm, "end": v(6.77, 2.74) * mm});
            skLineSegment(sketch, "E405", {"start": v(6.77, 2.74) * mm, "end": v(7.84, 3.25) * mm});
            skLineSegment(sketch, "E406", {"start": v(7.84, 3.25) * mm, "end": v(8.8, 3.46) * mm});
            skLineSegment(sketch, "E407", {"start": v(8.8, 3.46) * mm, "end": v(9.13, 3.46) * mm});
            skLineSegment(sketch, "E408", {"start": v(9.13, 3.46) * mm, "end": v(9.42, 3.46) * mm});
            skLineSegment(sketch, "E409", {"start": v(9.42, 3.46) * mm, "end": v(10.3, 3.29) * mm});
            skLineSegment(sketch, "E410", {"start": v(10.3, 3.29) * mm, "end": v(11.05, 2.88) * mm});
            skLineSegment(sketch, "E411", {"start": v(11.05, 2.88) * mm, "end": v(11.17, 2.76) * mm});
            skLineSegment(sketch, "E412", {"start": v(11.17, 2.76) * mm, "end": v(11.3, 2.65) * mm});
            skLineSegment(sketch, "E413", {"start": v(11.3, 2.65) * mm, "end": v(11.72, 1.92) * mm});
            skLineSegment(sketch, "E414", {"start": v(11.72, 1.92) * mm, "end": v(11.9, 1.08) * mm});
            skLineSegment(sketch, "E415", {"start": v(11.9, 1.08) * mm, "end": v(11.9, 0.8) * mm});
            skLineSegment(sketch, "E416", {"start": v(11.9, 0.8) * mm, "end": v(11.9, -1.91) * mm});
            skLineSegment(sketch, "E417", {"start": v(11.9, -1.91) * mm, "end": v(11.9, -1.99) * mm});
            skLineSegment(sketch, "E418", {"start": v(11.9, -1.99) * mm, "end": v(11.99, -2.2) * mm});
            skLineSegment(sketch, "E419", {"start": v(11.99, -2.2) * mm, "end": v(12.2, -2.32) * mm});
            skLineSegment(sketch, "E420", {"start": v(12.2, -2.32) * mm, "end": v(12.25, -2.32) * mm});
            skLineSegment(sketch, "E421", {"start": v(12.25, -2.32) * mm, "end": v(12.25, -3.28) * mm});
            skLineSegment(sketch, "E422", {"start": v(12.25, -3.28) * mm, "end": v(12.22, -3.29) * mm});
            skLineSegment(sketch, "E423", {"start": v(12.22, -3.29) * mm, "end": v(11.98, -3.32) * mm});
            skLineSegment(sketch, "E424", {"start": v(11.98, -3.32) * mm, "end": v(11.96, -3.32) * mm});
            skLineSegment(sketch, "E425", {"start": v(11.96, -3.32) * mm, "end": v(11.94, -3.32) * mm});
            skLineSegment(sketch, "E426", {"start": v(11.94, -3.32) * mm, "end": v(11.78, -3.33) * mm});
            skLineSegment(sketch, "E427", {"start": v(11.78, -3.33) * mm, "end": v(11.72, -3.33) * mm});
            skLineSegment(sketch, "E428", {"start": v(11.72, -3.33) * mm, "end": v(11.59, -3.33) * mm});
            skLineSegment(sketch, "E429", {"start": v(11.59, -3.33) * mm, "end": v(11.23, -3.17) * mm});
            skLineSegment(sketch, "E430", {"start": v(11.23, -3.17) * mm, "end": v(11.2, -3.14) * mm});
            skLineSegment(sketch, "E431", {"start": v(11.2, -3.14) * mm, "end": v(11.16, -3.1) * mm});
            skLineSegment(sketch, "E432", {"start": v(11.16, -3.1) * mm, "end": v(10.97, -2.7) * mm});
            skLineSegment(sketch, "E433", {"start": v(10.97, -2.7) * mm, "end": v(10.96, -2.66) * mm});
            skLineSegment(sketch, "E434", {"start": v(10.96, -2.66) * mm, "end": v(10.93, -2.2) * mm});
            skLineSegment(sketch, "E435", {"start": v(10.93, -2.2) * mm, "end": v(10.86, -2.29) * mm});
            skLineSegment(sketch, "E436", {"start": v(10.86, -2.29) * mm, "end": v(9.92, -3.05) * mm});
            skLineSegment(sketch, "E437", {"start": v(9.92, -3.05) * mm, "end": v(9.81, -3.1) * mm});
            skLineSegment(sketch, "E438", {"start": v(9.81, -3.1) * mm, "end": v(9.7, -3.15) * mm});
            skLineSegment(sketch, "E439", {"start": v(9.7, -3.15) * mm, "end": v(8.7, -3.4) * mm});
            skLineSegment(sketch, "E440", {"start": v(8.7, -3.4) * mm, "end": v(8.36, -3.4) * mm});
            skLineSegment(sketch, "E441", {"start": v(8.65, -2.57) * mm, "end": v(8.93, -2.57) * mm});
            skLineSegment(sketch, "E442", {"start": v(8.93, -2.57) * mm, "end": v(9.67, -2.39) * mm});
            skLineSegment(sketch, "E443", {"start": v(9.67, -2.39) * mm, "end": v(9.76, -2.35) * mm});
            skLineSegment(sketch, "E444", {"start": v(9.76, -2.35) * mm, "end": v(9.84, -2.31) * mm});
            skLineSegment(sketch, "E445", {"start": v(9.84, -2.31) * mm, "end": v(10.5, -1.82) * mm});
            skLineSegment(sketch, "E446", {"start": v(10.5, -1.82) * mm, "end": v(10.54, -1.76) * mm});
            skLineSegment(sketch, "E447", {"start": v(10.54, -1.76) * mm, "end": v(10.58, -1.72) * mm});
            skLineSegment(sketch, "E448", {"start": v(10.58, -1.72) * mm, "end": v(10.78, -1.38) * mm});
            skLineSegment(sketch, "E449", {"start": v(10.78, -1.38) * mm, "end": v(10.78, -1.26) * mm});
            skLineSegment(sketch, "E450", {"start": v(10.78, -1.26) * mm, "end": v(10.78, -0.29) * mm});
            skLineSegment(sketch, "E451", {"start": v(10.78, -0.29) * mm, "end": v(10.65, -0.23) * mm});
            skLineSegment(sketch, "E452", {"start": v(10.65, -0.23) * mm, "end": v(9.48, 0.03) * mm});
            skLineSegment(sketch, "E453", {"start": v(9.48, 0.03) * mm, "end": v(9.1, 0.03) * mm});
            skLineSegment(sketch, "E454", {"start": v(9.1, 0.03) * mm, "end": v(8.75, 0.03) * mm});
            skLineSegment(sketch, "E455", {"start": v(8.75, 0.03) * mm, "end": v(7.81, -0.27) * mm});
            skLineSegment(sketch, "E456", {"start": v(7.81, -0.27) * mm, "end": v(7.73, -0.32) * mm});
            skLineSegment(sketch, "E457", {"start": v(7.73, -0.32) * mm, "end": v(7.64, -0.38) * mm});
            skLineSegment(sketch, "E458", {"start": v(7.64, -0.38) * mm, "end": v(7.33, -0.73) * mm});
            skLineSegment(sketch, "E459", {"start": v(7.33, -0.73) * mm, "end": v(7.2, -1.12) * mm});
            skLineSegment(sketch, "E460", {"start": v(7.2, -1.12) * mm, "end": v(7.2, -1.25) * mm});
            skLineSegment(sketch, "E461", {"start": v(7.2, -1.25) * mm, "end": v(7.2, -1.38) * mm});
            skLineSegment(sketch, "E462", {"start": v(7.2, -1.38) * mm, "end": v(7.3, -1.73) * mm});
            skLineSegment(sketch, "E463", {"start": v(7.3, -1.73) * mm, "end": v(7.3, -1.77) * mm});
            skLineSegment(sketch, "E464", {"start": v(7.3, -1.77) * mm, "end": v(7.33, -1.81) * mm});
            skLineSegment(sketch, "E465", {"start": v(7.33, -1.81) * mm, "end": v(7.58, -2.16) * mm});
            skLineSegment(sketch, "E466", {"start": v(7.58, -2.16) * mm, "end": v(7.61, -2.2) * mm});
            skLineSegment(sketch, "E467", {"start": v(7.61, -2.2) * mm, "end": v(7.65, -2.22) * mm});
            skLineSegment(sketch, "E468", {"start": v(7.65, -2.22) * mm, "end": v(8.03, -2.45) * mm});
            skLineSegment(sketch, "E469", {"start": v(8.03, -2.45) * mm, "end": v(8.08, -2.47) * mm});
            skLineSegment(sketch, "E470", {"start": v(8.08, -2.47) * mm, "end": v(8.12, -2.49) * mm});
            skLineSegment(sketch, "E471", {"start": v(8.12, -2.49) * mm, "end": v(8.52, -2.57) * mm});
            skLineSegment(sketch, "E472", {"start": v(8.52, -2.57) * mm, "end": v(8.65, -2.57) * mm});
            skLineSegment(sketch, "E473", {"start": v(17.1, -3.4) * mm, "end": v(16.74, -3.4) * mm});
            skLineSegment(sketch, "E474", {"start": v(16.74, -3.4) * mm, "end": v(15.79, -3.1) * mm});
            skLineSegment(sketch, "E475", {"start": v(15.79, -3.1) * mm, "end": v(15.68, -3.03) * mm});
            skLineSegment(sketch, "E476", {"start": v(15.68, -3.03) * mm, "end": v(15.58, -2.96) * mm});
            skLineSegment(sketch, "E477", {"start": v(15.58, -2.96) * mm, "end": v(14.74, -2.14) * mm});
            skLineSegment(sketch, "E478", {"start": v(14.74, -2.14) * mm, "end": v(14.68, -2.04) * mm});
            skLineSegment(sketch, "E479", {"start": v(14.68, -2.04) * mm, "end": v(14.68, -3.28) * mm});
            skLineSegment(sketch, "E480", {"start": v(14.68, -3.28) * mm, "end": v(13.7, -3.28) * mm});
            skLineSegment(sketch, "E481", {"start": v(13.7, -3.28) * mm, "end": v(13.7, 5.99) * mm});
            skLineSegment(sketch, "E482", {"start": v(13.7, 5.99) * mm, "end": v(14.8, 5.99) * mm});
            skLineSegment(sketch, "E483", {"start": v(14.8, 5.99) * mm, "end": v(14.8, 2.03) * mm});
            skLineSegment(sketch, "E484", {"start": v(14.8, 2.03) * mm, "end": v(14.88, 2.13) * mm});
            skLineSegment(sketch, "E485", {"start": v(14.88, 2.13) * mm, "end": v(15.73, 3) * mm});
            skLineSegment(sketch, "E486", {"start": v(15.73, 3) * mm, "end": v(15.84, 3.07) * mm});
            skLineSegment(sketch, "E487", {"start": v(15.84, 3.07) * mm, "end": v(15.94, 3.13) * mm});
            skLineSegment(sketch, "E488", {"start": v(15.94, 3.13) * mm, "end": v(16.93, 3.46) * mm});
            skLineSegment(sketch, "E489", {"start": v(16.93, 3.46) * mm, "end": v(17.26, 3.46) * mm});
            skLineSegment(sketch, "E490", {"start": v(17.26, 3.46) * mm, "end": v(17.57, 3.46) * mm});
            skLineSegment(sketch, "E491", {"start": v(17.57, 3.46) * mm, "end": v(18.4, 3.22) * mm});
            skLineSegment(sketch, "E492", {"start": v(18.4, 3.22) * mm, "end": v(18.5, 3.17) * mm});
            skLineSegment(sketch, "E493", {"start": v(18.5, 3.17) * mm, "end": v(18.58, 3.12) * mm});
            skLineSegment(sketch, "E494", {"start": v(18.58, 3.12) * mm, "end": v(19.36, 2.48) * mm});
            skLineSegment(sketch, "E495", {"start": v(19.36, 2.48) * mm, "end": v(19.43, 2.4) * mm});
            skLineSegment(sketch, "E496", {"start": v(19.43, 2.4) * mm, "end": v(19.49, 2.32) * mm});
            skLineSegment(sketch, "E497", {"start": v(19.49, 2.32) * mm, "end": v(19.99, 1.4) * mm});
            skLineSegment(sketch, "E498", {"start": v(19.99, 1.4) * mm, "end": v(20.02, 1.3) * mm});
            skLineSegment(sketch, "E499", {"start": v(20.02, 1.3) * mm, "end": v(20.06, 1.19) * mm});
            skLineSegment(sketch, "E500", {"start": v(20.06, 1.19) * mm, "end": v(20.23, 0.3) * mm});
            skLineSegment(sketch, "E501", {"start": v(20.23, 0.3) * mm, "end": v(20.23, 0) * mm});
            skLineSegment(sketch, "E502", {"start": v(20.23, 0) * mm, "end": v(20.23, -0.32) * mm});
            skLineSegment(sketch, "E503", {"start": v(20.23, -0.32) * mm, "end": v(20.03, -1.21) * mm});
            skLineSegment(sketch, "E504", {"start": v(20.03, -1.21) * mm, "end": v(19.99, -1.32) * mm});
            skLineSegment(sketch, "E505", {"start": v(19.99, -1.32) * mm, "end": v(19.95, -1.42) * mm});
            skLineSegment(sketch, "E506", {"start": v(19.95, -1.42) * mm, "end": v(19.4, -2.32) * mm});
            skLineSegment(sketch, "E507", {"start": v(19.4, -2.32) * mm, "end": v(19.33, -2.4) * mm});
            skLineSegment(sketch, "E508", {"start": v(19.33, -2.4) * mm, "end": v(19.26, -2.48) * mm});
            skLineSegment(sketch, "E509", {"start": v(19.26, -2.48) * mm, "end": v(18.43, -3.1) * mm});
            skLineSegment(sketch, "E510", {"start": v(18.43, -3.1) * mm, "end": v(18.33, -3.14) * mm});
            skLineSegment(sketch, "E511", {"start": v(18.33, -3.14) * mm, "end": v(18.24, -3.18) * mm});
            skLineSegment(sketch, "E512", {"start": v(18.24, -3.18) * mm, "end": v(17.38, -3.4) * mm});
            skLineSegment(sketch, "E513", {"start": v(17.38, -3.4) * mm, "end": v(17.1, -3.4) * mm});
            skLineSegment(sketch, "E514", {"start": v(16.81, -2.45) * mm, "end": v(17.04, -2.45) * mm});
            skLineSegment(sketch, "E515", {"start": v(17.04, -2.45) * mm, "end": v(17.66, -2.27) * mm});
            skLineSegment(sketch, "E516", {"start": v(17.66, -2.27) * mm, "end": v(17.73, -2.24) * mm});
            skLineSegment(sketch, "E517", {"start": v(17.73, -2.24) * mm, "end": v(17.8, -2.2) * mm});
            skLineSegment(sketch, "E518", {"start": v(17.8, -2.2) * mm, "end": v(18.4, -1.75) * mm});
            skLineSegment(sketch, "E519", {"start": v(18.4, -1.75) * mm, "end": v(18.45, -1.7) * mm});
            skLineSegment(sketch, "E520", {"start": v(18.45, -1.7) * mm, "end": v(18.5, -1.64) * mm});
            skLineSegment(sketch, "E521", {"start": v(18.5, -1.64) * mm, "end": v(18.9, -0.99) * mm});
            skLineSegment(sketch, "E522", {"start": v(18.9, -0.99) * mm, "end": v(18.92, -0.91) * mm});
            skLineSegment(sketch, "E523", {"start": v(18.92, -0.91) * mm, "end": v(18.95, -0.84) * mm});
            skLineSegment(sketch, "E524", {"start": v(18.95, -0.84) * mm, "end": v(19.09, -0.2) * mm});
            skLineSegment(sketch, "E525", {"start": v(19.09, -0.2) * mm, "end": v(19.09, 0) * mm});
            skLineSegment(sketch, "E526", {"start": v(19.09, 0) * mm, "end": v(19.09, 0.24) * mm});
            skLineSegment(sketch, "E527", {"start": v(19.09, 0.24) * mm, "end": v(18.96, 0.86) * mm});
            skLineSegment(sketch, "E528", {"start": v(18.96, 0.86) * mm, "end": v(18.93, 0.94) * mm});
            skLineSegment(sketch, "E529", {"start": v(18.93, 0.94) * mm, "end": v(18.9, 1.01) * mm});
            skLineSegment(sketch, "E530", {"start": v(18.9, 1.01) * mm, "end": v(18.53, 1.68) * mm});
            skLineSegment(sketch, "E531", {"start": v(18.53, 1.68) * mm, "end": v(18.49, 1.73) * mm});
            skLineSegment(sketch, "E532", {"start": v(18.49, 1.73) * mm, "end": v(18.44, 1.8) * mm});
            skLineSegment(sketch, "E533", {"start": v(18.44, 1.8) * mm, "end": v(17.86, 2.25) * mm});
            skLineSegment(sketch, "E534", {"start": v(17.86, 2.25) * mm, "end": v(17.8, 2.29) * mm});
            skLineSegment(sketch, "E535", {"start": v(17.8, 2.29) * mm, "end": v(17.73, 2.32) * mm});
            skLineSegment(sketch, "E536", {"start": v(17.73, 2.32) * mm, "end": v(17.12, 2.5) * mm});
            skLineSegment(sketch, "E537", {"start": v(17.12, 2.5) * mm, "end": v(16.92, 2.5) * mm});
            skLineSegment(sketch, "E538", {"start": v(16.92, 2.5) * mm, "end": v(16.75, 2.5) * mm});
            skLineSegment(sketch, "E539", {"start": v(16.75, 2.5) * mm, "end": v(16.3, 2.4) * mm});
            skLineSegment(sketch, "E540", {"start": v(16.3, 2.4) * mm, "end": v(16.24, 2.37) * mm});
            skLineSegment(sketch, "E541", {"start": v(16.24, 2.37) * mm, "end": v(16.19, 2.35) * mm});
            skLineSegment(sketch, "E542", {"start": v(16.19, 2.35) * mm, "end": v(15.7, 2.07) * mm});
            skLineSegment(sketch, "E543", {"start": v(15.7, 2.07) * mm, "end": v(15.65, 2.03) * mm});
            skLineSegment(sketch, "E544", {"start": v(15.65, 2.03) * mm, "end": v(15.6, 2) * mm});
            skLineSegment(sketch, "E545", {"start": v(15.6, 2) * mm, "end": v(15.2, 1.59) * mm});
            skLineSegment(sketch, "E546", {"start": v(15.2, 1.59) * mm, "end": v(15.17, 1.54) * mm});
            skLineSegment(sketch, "E547", {"start": v(15.17, 1.54) * mm, "end": v(15.13, 1.5) * mm});
            skLineSegment(sketch, "E548", {"start": v(15.13, 1.5) * mm, "end": v(14.83, 1) * mm});
            skLineSegment(sketch, "E549", {"start": v(14.83, 1) * mm, "end": v(14.8, 0.95) * mm});
            skLineSegment(sketch, "E550", {"start": v(14.8, 0.95) * mm, "end": v(14.8, -0.97) * mm});
            skLineSegment(sketch, "E551", {"start": v(14.8, -0.97) * mm, "end": v(14.82, -1.02) * mm});
            skLineSegment(sketch, "E552", {"start": v(14.82, -1.02) * mm, "end": v(15.05, -1.51) * mm});
            skLineSegment(sketch, "E553", {"start": v(15.05, -1.51) * mm, "end": v(15.08, -1.56) * mm});
            skLineSegment(sketch, "E554", {"start": v(15.08, -1.56) * mm, "end": v(15.12, -1.6) * mm});
            skLineSegment(sketch, "E555", {"start": v(15.12, -1.6) * mm, "end": v(15.53, -1.99) * mm});
            skLineSegment(sketch, "E556", {"start": v(15.53, -1.99) * mm, "end": v(15.58, -2.02) * mm});
            skLineSegment(sketch, "E557", {"start": v(15.58, -2.02) * mm, "end": v(15.62, -2.05) * mm});
            skLineSegment(sketch, "E558", {"start": v(15.62, -2.05) * mm, "end": v(16.13, -2.31) * mm});
            skLineSegment(sketch, "E559", {"start": v(16.13, -2.31) * mm, "end": v(16.19, -2.33) * mm});
            skLineSegment(sketch, "E560", {"start": v(16.19, -2.33) * mm, "end": v(16.24, -2.35) * mm});
            skLineSegment(sketch, "E561", {"start": v(16.24, -2.35) * mm, "end": v(16.67, -2.45) * mm});
            skLineSegment(sketch, "E562", {"start": v(16.67, -2.45) * mm, "end": v(16.81, -2.45) * mm});
            skLineSegment(sketch, "E563", {"start": v(24.5, -3.4) * mm, "end": v(24.16, -3.4) * mm});
            skLineSegment(sketch, "E564", {"start": v(24.16, -3.4) * mm, "end": v(23.24, -3.18) * mm});
            skLineSegment(sketch, "E565", {"start": v(23.24, -3.18) * mm, "end": v(23.13, -3.13) * mm});
            skLineSegment(sketch, "E566", {"start": v(23.13, -3.13) * mm, "end": v(23.03, -3.08) * mm});
            skLineSegment(sketch, "E567", {"start": v(23.03, -3.08) * mm, "end": v(22.15, -2.46) * mm});
            skLineSegment(sketch, "E568", {"start": v(22.15, -2.46) * mm, "end": v(22.08, -2.38) * mm});
            skLineSegment(sketch, "E569", {"start": v(22.08, -2.38) * mm, "end": v(22, -2.3) * mm});
            skLineSegment(sketch, "E570", {"start": v(22, -2.3) * mm, "end": v(21.44, -1.4) * mm});
            skLineSegment(sketch, "E571", {"start": v(21.44, -1.4) * mm, "end": v(21.4, -1.29) * mm});
            skLineSegment(sketch, "E572", {"start": v(21.4, -1.29) * mm, "end": v(21.36, -1.18) * mm});
            skLineSegment(sketch, "E573", {"start": v(21.36, -1.18) * mm, "end": v(21.16, -0.28) * mm});
            skLineSegment(sketch, "E574", {"start": v(21.16, -0.28) * mm, "end": v(21.16, 0.02) * mm});
            skLineSegment(sketch, "E575", {"start": v(21.16, 0.02) * mm, "end": v(21.16, 0.35) * mm});
            skLineSegment(sketch, "E576", {"start": v(21.16, 0.35) * mm, "end": v(21.37, 1.24) * mm});
            skLineSegment(sketch, "E577", {"start": v(21.37, 1.24) * mm, "end": v(21.4, 1.34) * mm});
            skLineSegment(sketch, "E578", {"start": v(21.4, 1.34) * mm, "end": v(21.45, 1.44) * mm});
            skLineSegment(sketch, "E579", {"start": v(21.45, 1.44) * mm, "end": v(22.02, 2.35) * mm});
            skLineSegment(sketch, "E580", {"start": v(22.02, 2.35) * mm, "end": v(22.1, 2.43) * mm});
            skLineSegment(sketch, "E581", {"start": v(22.1, 2.43) * mm, "end": v(22.16, 2.51) * mm});
            skLineSegment(sketch, "E582", {"start": v(22.16, 2.51) * mm, "end": v(23.04, 3.14) * mm});
            skLineSegment(sketch, "E583", {"start": v(23.04, 3.14) * mm, "end": v(23.15, 3.18) * mm});
            skLineSegment(sketch, "E584", {"start": v(23.15, 3.18) * mm, "end": v(23.25, 3.23) * mm});
            skLineSegment(sketch, "E585", {"start": v(23.25, 3.23) * mm, "end": v(24.19, 3.46) * mm});
            skLineSegment(sketch, "E586", {"start": v(24.19, 3.46) * mm, "end": v(24.5, 3.46) * mm});
            skLineSegment(sketch, "E587", {"start": v(24.5, 3.46) * mm, "end": v(24.84, 3.46) * mm});
            skLineSegment(sketch, "E588", {"start": v(24.84, 3.46) * mm, "end": v(25.75, 3.23) * mm});
            skLineSegment(sketch, "E589", {"start": v(25.75, 3.23) * mm, "end": v(25.86, 3.18) * mm});
            skLineSegment(sketch, "E590", {"start": v(25.86, 3.18) * mm, "end": v(25.96, 3.14) * mm});
            skLineSegment(sketch, "E591", {"start": v(25.96, 3.14) * mm, "end": v(26.84, 2.51) * mm});
            skLineSegment(sketch, "E592", {"start": v(26.84, 2.51) * mm, "end": v(26.92, 2.43) * mm});
            skLineSegment(sketch, "E593", {"start": v(26.92, 2.43) * mm, "end": v(27, 2.35) * mm});
            skLineSegment(sketch, "E594", {"start": v(27, 2.35) * mm, "end": v(27.56, 1.44) * mm});
            skLineSegment(sketch, "E595", {"start": v(27.56, 1.44) * mm, "end": v(27.6, 1.34) * mm});
            skLineSegment(sketch, "E596", {"start": v(27.6, 1.34) * mm, "end": v(27.64, 1.24) * mm});
            skLineSegment(sketch, "E597", {"start": v(27.64, 1.24) * mm, "end": v(27.85, 0.32) * mm});
            skLineSegment(sketch, "E598", {"start": v(27.85, 0.32) * mm, "end": v(27.85, 0.02) * mm});
            skLineSegment(sketch, "E599", {"start": v(27.85, 0.02) * mm, "end": v(27.85, -0.3) * mm});
            skLineSegment(sketch, "E600", {"start": v(27.85, -0.3) * mm, "end": v(27.65, -1.18) * mm});
            skLineSegment(sketch, "E601", {"start": v(27.65, -1.18) * mm, "end": v(27.61, -1.29) * mm});
            skLineSegment(sketch, "E602", {"start": v(27.61, -1.29) * mm, "end": v(27.57, -1.4) * mm});
            skLineSegment(sketch, "E603", {"start": v(27.57, -1.4) * mm, "end": v(27, -2.3) * mm});
            skLineSegment(sketch, "E604", {"start": v(27, -2.3) * mm, "end": v(26.92, -2.38) * mm});
            skLineSegment(sketch, "E605", {"start": v(26.92, -2.38) * mm, "end": v(26.85, -2.46) * mm});
            skLineSegment(sketch, "E606", {"start": v(26.85, -2.46) * mm, "end": v(25.97, -3.08) * mm});
            skLineSegment(sketch, "E607", {"start": v(25.97, -3.08) * mm, "end": v(25.86, -3.13) * mm});
            skLineSegment(sketch, "E608", {"start": v(25.86, -3.13) * mm, "end": v(25.76, -3.18) * mm});
            skLineSegment(sketch, "E609", {"start": v(25.76, -3.18) * mm, "end": v(24.81, -3.4) * mm});
            skLineSegment(sketch, "E610", {"start": v(24.81, -3.4) * mm, "end": v(24.5, -3.4) * mm});
            skLineSegment(sketch, "E611", {"start": v(22.3, 0) * mm, "end": v(22.3, -0.23) * mm});
            skLineSegment(sketch, "E612", {"start": v(22.3, -0.23) * mm, "end": v(22.44, -0.88) * mm});
            skLineSegment(sketch, "E613", {"start": v(22.44, -0.88) * mm, "end": v(22.47, -0.96) * mm});
            skLineSegment(sketch, "E614", {"start": v(22.47, -0.96) * mm, "end": v(22.5, -1.03) * mm});
            skLineSegment(sketch, "E615", {"start": v(22.5, -1.03) * mm, "end": v(22.9, -1.68) * mm});
            skLineSegment(sketch, "E616", {"start": v(22.9, -1.68) * mm, "end": v(22.94, -1.73) * mm});
            skLineSegment(sketch, "E617", {"start": v(22.94, -1.73) * mm, "end": v(23, -1.79) * mm});
            skLineSegment(sketch, "E618", {"start": v(23, -1.79) * mm, "end": v(23.57, -2.22) * mm});
            skLineSegment(sketch, "E619", {"start": v(23.57, -2.22) * mm, "end": v(23.64, -2.26) * mm});
            skLineSegment(sketch, "E620", {"start": v(23.64, -2.26) * mm, "end": v(23.7, -2.29) * mm});
            skLineSegment(sketch, "E621", {"start": v(23.7, -2.29) * mm, "end": v(24.3, -2.45) * mm});
            skLineSegment(sketch, "E622", {"start": v(24.3, -2.45) * mm, "end": v(24.5, -2.45) * mm});
            skLineSegment(sketch, "E623", {"start": v(24.5, -2.45) * mm, "end": v(24.71, -2.45) * mm});
            skLineSegment(sketch, "E624", {"start": v(24.71, -2.45) * mm, "end": v(25.29, -2.29) * mm});
            skLineSegment(sketch, "E625", {"start": v(25.29, -2.29) * mm, "end": v(25.36, -2.26) * mm});
            skLineSegment(sketch, "E626", {"start": v(25.36, -2.26) * mm, "end": v(25.42, -2.22) * mm});
            skLineSegment(sketch, "E627", {"start": v(25.42, -2.22) * mm, "end": v(26, -1.78) * mm});
            skLineSegment(sketch, "E628", {"start": v(26, -1.78) * mm, "end": v(26.06, -1.73) * mm});
            skLineSegment(sketch, "E629", {"start": v(26.06, -1.73) * mm, "end": v(26.11, -1.67) * mm});
            skLineSegment(sketch, "E630", {"start": v(26.11, -1.67) * mm, "end": v(26.5, -1.01) * mm});
            skLineSegment(sketch, "E631", {"start": v(26.5, -1.01) * mm, "end": v(26.54, -0.94) * mm});
            skLineSegment(sketch, "E632", {"start": v(26.54, -0.94) * mm, "end": v(26.56, -0.86) * mm});
            skLineSegment(sketch, "E633", {"start": v(26.56, -0.86) * mm, "end": v(26.7, -0.2) * mm});
            skLineSegment(sketch, "E634", {"start": v(26.7, -0.2) * mm, "end": v(26.7, 0.03) * mm});
            skLineSegment(sketch, "E635", {"start": v(26.7, 0.03) * mm, "end": v(26.7, 0.27) * mm});
            skLineSegment(sketch, "E636", {"start": v(26.7, 0.27) * mm, "end": v(26.56, 0.92) * mm});
            skLineSegment(sketch, "E637", {"start": v(26.56, 0.92) * mm, "end": v(26.54, 1) * mm});
            skLineSegment(sketch, "E638", {"start": v(26.54, 1) * mm, "end": v(26.5, 1.07) * mm});
            skLineSegment(sketch, "E639", {"start": v(26.5, 1.07) * mm, "end": v(26.11, 1.72) * mm});
            skLineSegment(sketch, "E640", {"start": v(26.11, 1.72) * mm, "end": v(26.06, 1.78) * mm});
            skLineSegment(sketch, "E641", {"start": v(26.06, 1.78) * mm, "end": v(26, 1.83) * mm});
            skLineSegment(sketch, "E642", {"start": v(26, 1.83) * mm, "end": v(25.42, 2.27) * mm});
            skLineSegment(sketch, "E643", {"start": v(25.42, 2.27) * mm, "end": v(25.36, 2.3) * mm});
            skLineSegment(sketch, "E644", {"start": v(25.36, 2.3) * mm, "end": v(25.29, 2.34) * mm});
            skLineSegment(sketch, "E645", {"start": v(25.29, 2.34) * mm, "end": v(24.7, 2.5) * mm});
            skLineSegment(sketch, "E646", {"start": v(24.7, 2.5) * mm, "end": v(24.5, 2.5) * mm});
            skLineSegment(sketch, "E647", {"start": v(24.5, 2.5) * mm, "end": v(24.28, 2.5) * mm});
            skLineSegment(sketch, "E648", {"start": v(24.28, 2.5) * mm, "end": v(23.7, 2.33) * mm});
            skLineSegment(sketch, "E649", {"start": v(23.7, 2.33) * mm, "end": v(23.64, 2.3) * mm});
            skLineSegment(sketch, "E650", {"start": v(23.64, 2.3) * mm, "end": v(23.57, 2.27) * mm});
            skLineSegment(sketch, "E651", {"start": v(23.57, 2.27) * mm, "end": v(23, 1.82) * mm});
            skLineSegment(sketch, "E652", {"start": v(23, 1.82) * mm, "end": v(22.94, 1.76) * mm});
            skLineSegment(sketch, "E653", {"start": v(22.94, 1.76) * mm, "end": v(22.9, 1.7) * mm});
            skLineSegment(sketch, "E654", {"start": v(22.9, 1.7) * mm, "end": v(22.5, 1.05) * mm});
            skLineSegment(sketch, "E655", {"start": v(22.5, 1.05) * mm, "end": v(22.47, 0.98) * mm});
            skLineSegment(sketch, "E656", {"start": v(22.47, 0.98) * mm, "end": v(22.44, 0.9) * mm});
            skLineSegment(sketch, "E657", {"start": v(22.44, 0.9) * mm, "end": v(22.3, 0.23) * mm});
            skLineSegment(sketch, "E658", {"start": v(22.3, 0.23) * mm, "end": v(22.3, 0) * mm});
            skSolve(sketch);
        }
        {
            var Q0;
            Q0 = qSketchRegion(id + "F0", true);
            extrude(context, id + "F1", {"entities" : qUnion([Q0]), "depth" : 1.27 * mm, "offsetDistance" : 25.4 * mm});
        }
        {
            var Q0;
            Q0=qCreatedBy(makeId("Right.planeOp"),FACE);
            var sketch = newSketch(context, id + "F2", { "sketchPlane" : qUnion([Q0])});
            skLineSegment(sketch, "E659.bottom", {"start": v(-23.16, -2.99) * mm, "end": v(23.33, -2.99) * mm});
            skLineSegment(sketch, "E659.top", {"start": v(-23.16, -3.34) * mm, "end": v(23.33, -3.34) * mm});
            skLineSegment(sketch, "E659.left", {"start": v(-23.16, -2.99) * mm, "end": v(-23.16, -3.34) * mm});
            skLineSegment(sketch, "E659.right", {"start": v(23.33, -2.99) * mm, "end": v(23.33, -3.34) * mm});
            skLineSegment(sketch, "E660.bottom", {"start": v(-11.7, 4.7) * mm, "end": v(-11.41, 4.7) * mm});
            skLineSegment(sketch, "E660.top", {"start": v(-11.7, 3.15) * mm, "end": v(-11.41, 3.15) * mm});
            skLineSegment(sketch, "E660.left", {"start": v(-11.7, 4.7) * mm, "end": v(-11.7, 3.15) * mm});
            skLineSegment(sketch, "E660.right", {"start": v(-11.41, 4.7) * mm, "end": v(-11.41, 3.15) * mm});
            skSolve(sketch);
        }
        {
            var Q0;
            Q0 = qSketchRegion(id + "F2", true);
            extrude(context, id + "F3", {"entities" : qUnion([Q0]), "depth" : 0.5 * mm, "offsetDistance" : 25.4 * mm});
        }
        {
            var Q0;
            Q0=qCreatedBy(makeId("Right.planeOp"),FACE);
            var sketch = newSketch(context, id + "F4", { "sketchPlane" : qUnion([Q0])});
            skLineSegment(sketch, "E661.bottom", {"start": v(-27.56, -5.9) * mm, "end": v(27.05, -5.9) * mm});
            skLineSegment(sketch, "E661.top", {"start": v(-27.56, -6.3) * mm, "end": v(27.05, -6.3) * mm});
            skLineSegment(sketch, "E661.left", {"start": v(-27.56, -5.9) * mm, "end": v(-27.56, -6.3) * mm});
            skLineSegment(sketch, "E661.right", {"start": v(27.05, -5.9) * mm, "end": v(27.05, -6.3) * mm});
            skSolve(sketch);
        }
        {
            var Q0;
            Q0=makeQuery(id+"F4.imprint","IMPRINT",FACE,{"disambiguationData":[TD([[makeQuery(id+"F4.imprint","IMPRINT",EDGE,{"derivedFrom":sQuery(id+"F4.wireOp",EDGE,"E661.bottom")}),-1.0]])]});
            extrude(context, id + "F5", {"entities" : qUnion([Q0]), "depth" : 6.35 * mm, "offsetDistance" : 25.4 * mm});
        }
    });
